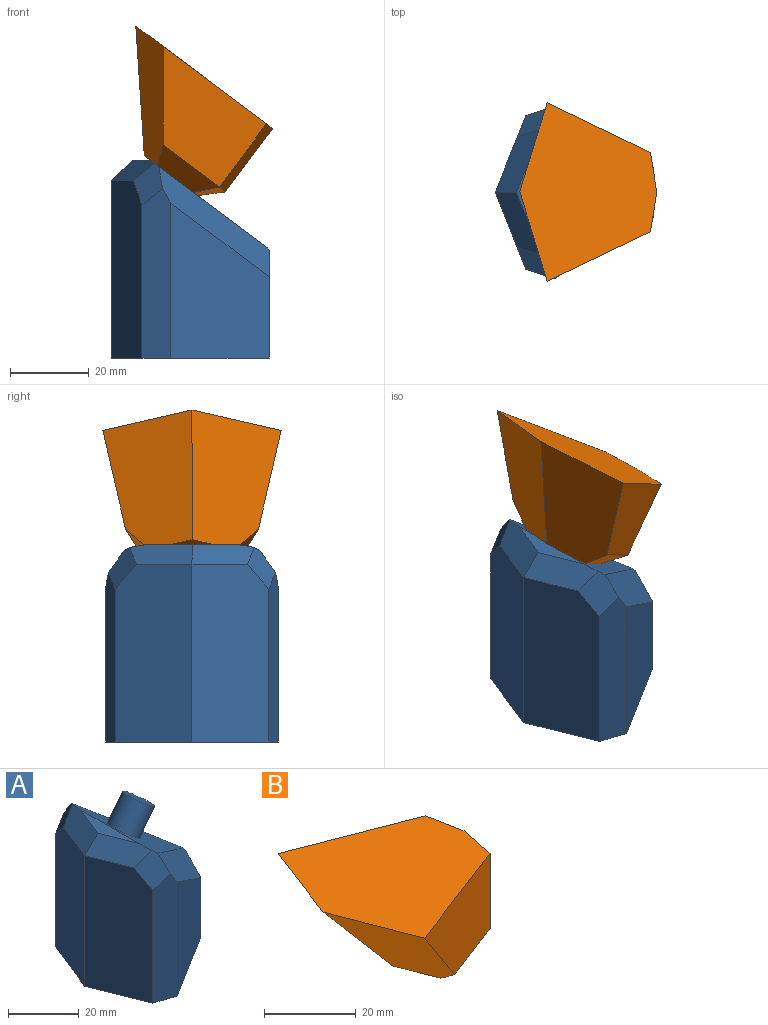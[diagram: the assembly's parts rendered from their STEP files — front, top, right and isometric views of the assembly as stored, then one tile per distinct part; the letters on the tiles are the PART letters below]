
ASSEMBLY  parts=2 mates=1
PART A: 18 faces, bbox 40x43.7x56.9 mm
  f0: plane 43.66x40mm, normal (0,0,-1), area 1152.3mm2, adj f1,f2,f3,f4,f7,f10,f15
  f1: plane 39.24x24.93mm, normal (0.53,-0.85,0), area 878.9mm2, adj f0,f10,f13,f15
  f2: plane 39.24x24.93mm, normal (0.53,0.85,0), area 878.9mm2, adj f0,f7,f14,f15
  f3: plane 45x19.45mm, normal (-0.93,0.37,0), area 924.2mm2, adj f0,f4,f7,f8,f12
  f4: plane 45x19.45mm, normal (-0.93,-0.37,0), area 924.2mm2, adj f0,f3,f9,f10,f11
  f5: plane 23.07x4.62mm, normal (0,0,1), area 53.2mm2, adj f6,f8,f9
  f6: plane 34.32x29.51mm, normal (0.6,0,0.8), area 588.2mm2, adj f5,f8,f9,f11,f12,f13,f14,f16
  f7: plane 42.9x7.29mm, normal (-0.31,0.95,0), area 313.6mm2, adj f0,f2,f3,f12,f14
  f8: plane 15.79x10.94mm, normal (-0.66,0.26,0.71), area 112.3mm2, adj f3,f5,f6,f9,f12
  f9: plane 15.79x10.94mm, normal (-0.66,-0.26,0.71), area 112.3mm2, adj f4,f5,f6,f8,f11
  f10: plane 42.9x7.29mm, normal (-0.31,-0.95,0), area 313.6mm2, adj f0,f1,f4,f11,f13
  f11: plane 10.6x7.37mm, normal (-0.57,-0.71,0.41), area 63.3mm2, adj f4,f6,f9,f10,f13
  f12: plane 10.6x7.37mm, normal (-0.57,0.71,0.41), area 63.3mm2, adj f3,f6,f7,f8,f14
  f13: plane 27.95x27.91mm, normal (0.7,-0.52,0.49), area 359.5mm2, adj f1,f6,f10,f11,f14,f15
  f14: plane 27.95x27.91mm, normal (0.7,0.52,0.49), area 359.5mm2, adj f2,f6,f7,f12,f13,f15
  f15: plane 27.17x12.5mm, normal (1,0,0), area 298.3mm2, adj f0,f1,f2,f13,f14
  f16: cylinder r=5mm len=14mm, axis (-0.6,0,-0.8), area 314.2mm2, adj f6,f17
  f17: plane 10x8mm, normal (0.6,0,0.8), area 78.5mm2, adj f16
PART B: 14 faces, bbox 43.3x45.1x25 mm
  f0: plane 32.67x20mm, normal (0.36,-0.93,0), area 540mm2, adj f3,f7,f8,f13
  f1: plane 32.67x20mm, normal (0.36,0.93,0), area 540mm2, adj f4,f7,f9,f10
  f2: plane 21.44x16.82mm, normal (0,0,-1), area 168.4mm2, adj f5,f8,f9,f10,f11,f12,f13
  f3: plane 20x10mm, normal (0.98,-0.2,0), area 204mm2, adj f0,f4,f7,f12
  f4: plane 20x10mm, normal (0.98,0.2,0), area 204mm2, adj f1,f3,f7,f11
  f5: cylinder r=5mm len=10mm, axis (0,0,-1), area 314.2mm2, adj f2,f6
  f6: plane 10x10mm, normal (0,0,-1), area 78.5mm2, adj f5
  f7: plane 45.13x43.35mm, normal (0,0,1), area 1279.6mm2, adj f0,f1,f3,f4,f8,f9
  f8: plane 25.55x25mm, normal (-0.73,-0.28,-0.62), area 634.9mm2, adj f0,f2,f7,f9,f13
  f9: plane 25.55x25mm, normal (-0.73,0.28,-0.62), area 634.9mm2, adj f1,f2,f7,f8,f10
  f10: plane 17.73x10.5mm, normal (0.25,0.66,-0.71), area 110.5mm2, adj f1,f2,f9,f11
  f11: plane 10x6.36mm, normal (0.69,0.14,-0.71), area 58.8mm2, adj f2,f4,f10,f12
  f12: plane 10x6.36mm, normal (0.69,-0.14,-0.71), area 58.8mm2, adj f2,f3,f11,f13
  f13: plane 17.73x10.5mm, normal (0.25,-0.66,-0.71), area 110.5mm2, adj f0,f2,f8,f12
PLACE A t=(30.75,0.47,32.05)mm
PLACE B rot(axis=(0,1,0),36.9deg) t=(34.65,0.47,79.12)mm
MATE fastened A.f16 <-> B.f5  axis (-0.6,0,-0.8) through (36.25,0.47,77.92)mm
